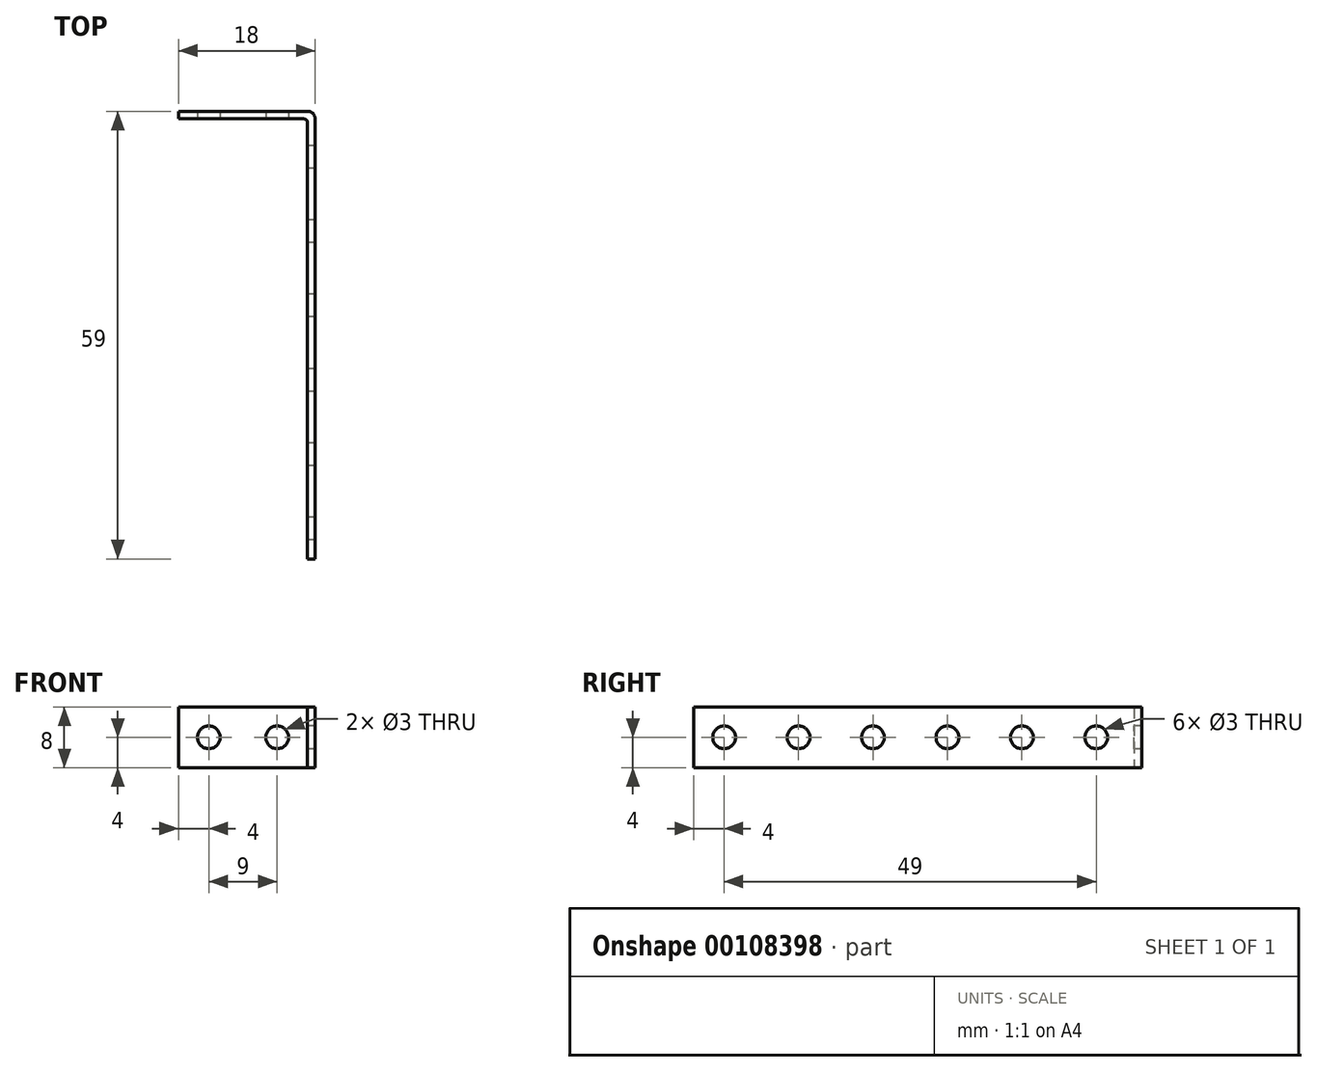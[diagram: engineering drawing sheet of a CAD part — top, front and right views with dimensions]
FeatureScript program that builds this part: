
annotation { "Feature Type Name" : "Feature", "Feature Type Description" : "" }
export const myFeature = defineFeature(function(context is Context, id is Id, definition is map)
    precondition{}
    {
        {
            var Q0;
            Q0=qCreatedBy(makeId("Top.planeOp"),FACE);
            var sketch = newSketch(context, id + "F0", { "sketchPlane" : qUnion([Q0])});
            skLineSegment(sketch, "E0.top", {"start": v(-0.5, -29) * mm, "end": v(0.5, -29) * mm});
            skLineSegment(sketch, "E0.left", {"start": v(-0.5, 29) * mm, "end": v(-0.5, -29) * mm});
            skLineSegment(sketch, "E0.right", {"start": v(0.5, 29) * mm, "end": v(0.5, -29) * mm});
            skPoint(sketch, "E0.middle", {"position": v(0, 0) * mm});
            skLineSegment(sketch, "E1.bottom", {"start": v(-0.5, 29) * mm, "end": v(-17.5, 29) * mm});
            skLineSegment(sketch, "E1.top", {"start": v(0.5, 30) * mm, "end": v(-17.5, 30) * mm});
            skLineSegment(sketch, "E1.left", {"start": v(0.5, 29) * mm, "end": v(0.5, 30) * mm});
            skLineSegment(sketch, "E1.right", {"start": v(-17.5, 29) * mm, "end": v(-17.5, 30) * mm});
            skSolve(sketch);
        }
        {
            var Q0;
            Q0 = qSketchRegion(id + "F0", true);
            extrude(context, id + "F1", {"entities" : qUnion([Q0]), "depth" : 8 * mm});
        }
        {
            var Q0;
            Q0=makeQuery(id+"F1.opExtrude","SWEPT_FACE",FACE,{"disambiguationData":[OSD([sQuery(id+"F0.wireOp",EDGE,"E0.left")])]});
            var sketch = newSketch(context, id + "F2", { "sketchPlane" : qUnion([Q0])});
            skLineSegment(sketch, "E2", {"start": v(29, 4) * mm, "end": v(25, 4) * mm});
            skCircle(sketch, "E3", {"center": v(25, 4) * mm, "radius": 1.5 * mm});
            skCircle(sketch, "E4.1.0.0", {"center": v(15.2, 4) * mm, "radius": 1.5 * mm});
            skCircle(sketch, "E4.2.0.0", {"center": v(5.4, 4) * mm, "radius": 1.5 * mm});
            skCircle(sketch, "E4.3.0.0", {"center": v(-4.4, 4) * mm, "radius": 1.5 * mm});
            skCircle(sketch, "E4.4.0.0", {"center": v(-14.2, 4) * mm, "radius": 1.5 * mm});
            skCircle(sketch, "E4.5.0.0", {"center": v(-24, 4) * mm, "radius": 1.5 * mm});
            skLineSegment(sketch, "E4.direction1", {"start": v(25, 4) * mm, "end": v(15.2, 4) * mm, "construction": true});
            skSolve(sketch);
        }
        {
            var Q0;
            Q0 = qSketchRegion(id + "F2", true);
            extrude(context, id + "F3", {"entities" : qUnion([Q0]), "operationType" : NewBodyOperationType.REMOVE, "oppositeDirection" : true, "depth" : 25 * mm});
        }
        {
            var Q0;
            Q0=makeQuery(id+"F1.opExtrude","SWEPT_FACE",FACE,{"disambiguationData":[OSD([sQuery(id+"F0.wireOp",EDGE,"E1.bottom")])]});
            var sketch = newSketch(context, id + "F4", { "sketchPlane" : qUnion([Q0])});
            skLineSegment(sketch, "E5", {"start": v(-0.5, 4) * mm, "end": v(-4.5, 4) * mm});
            skCircle(sketch, "E6", {"center": v(-4.5, 4) * mm, "radius": 1.5 * mm});
            skCircle(sketch, "E7.1.0.0", {"center": v(-13.5, 4) * mm, "radius": 1.5 * mm});
            skLineSegment(sketch, "E7.direction1", {"start": v(-4.5, 4) * mm, "end": v(-13.5, 4) * mm, "construction": true});
            skSolve(sketch);
        }
        {
            var Q0;
            Q0 = qSketchRegion(id + "F4", true);
            extrude(context, id + "F5", {"entities" : qUnion([Q0]), "operationType" : NewBodyOperationType.REMOVE, "oppositeDirection" : true, "depth" : 25 * mm});
        }
        {
            var Q0;
            Q0=makeQuery(id+"F1.opExtrude","SWEPT_EDGE",EDGE,{"disambiguationData":[OSD([sQuery(id+"F0.wireOp",EDGE,"E1.top"),sQuery(id+"F0.wireOp",EDGE,"E1.left")])]});
            fillet(context, id + "F6", {"entities" : qUnion([Q0]), "radius" : 1 * mm, "tangentPropagation" : true, "allowEdgeOverflow" : false});
        }
        {
            var Q0;
            Q0=makeQuery(id+"F1.opExtrude","SWEPT_EDGE",EDGE,{"disambiguationData":[OSD([sQuery(id+"F0.wireOp",EDGE,"E0.left"),sQuery(id+"F0.wireOp",EDGE,"E1.bottom")])]});
            fillet(context, id + "F7", {"entities" : qUnion([Q0]), "radius" : .5 * mm, "tangentPropagation" : true, "allowEdgeOverflow" : false});
        }
    });
